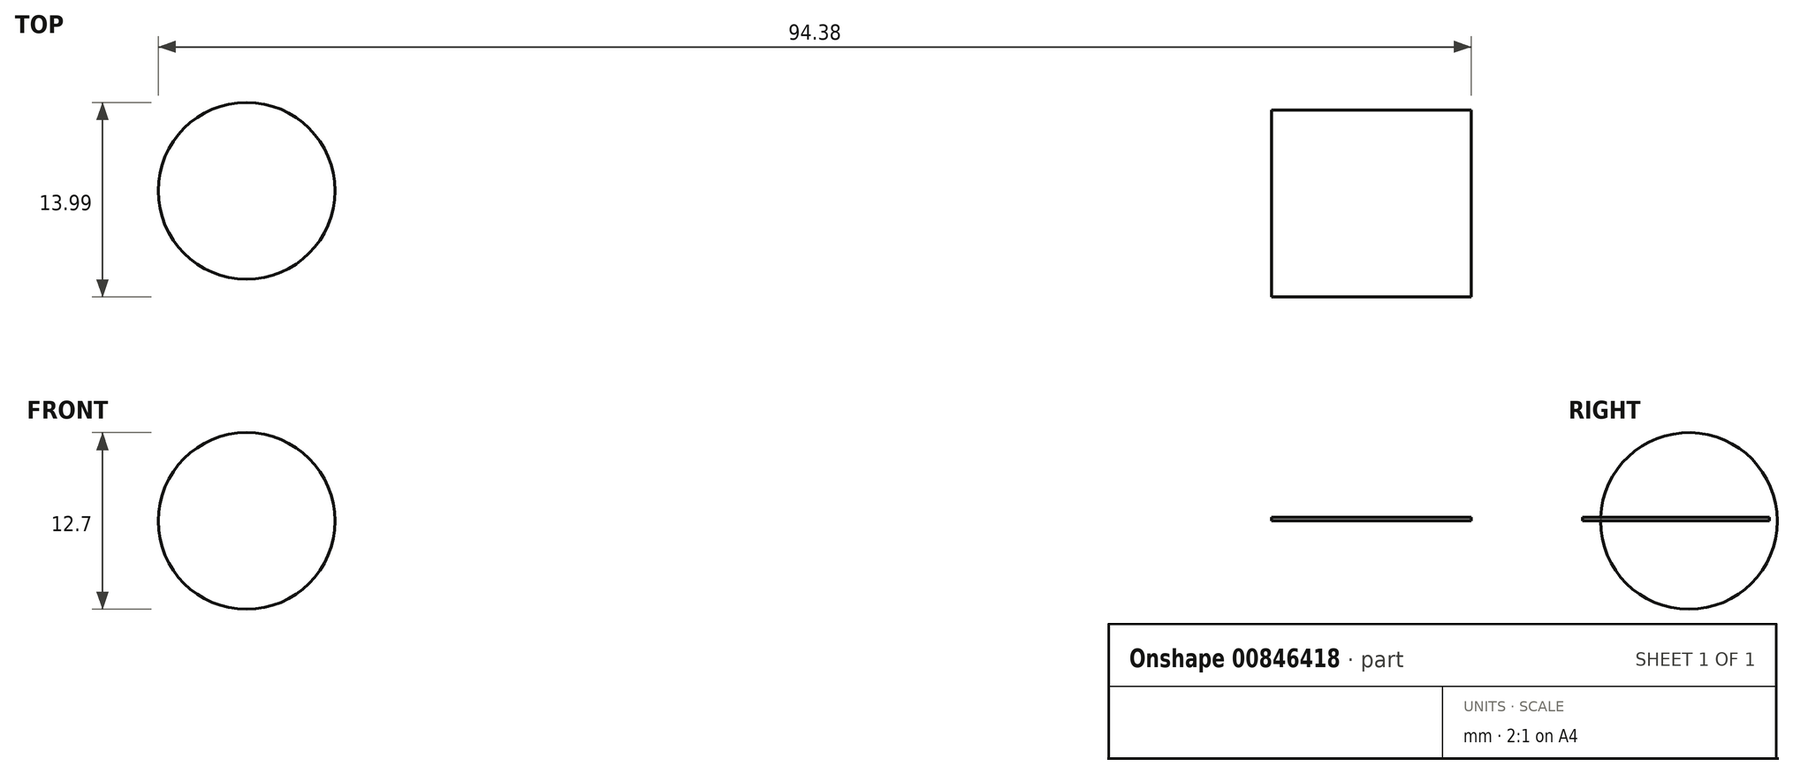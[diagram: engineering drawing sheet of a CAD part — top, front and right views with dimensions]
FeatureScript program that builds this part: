
annotation { "Feature Type Name" : "Feature", "Feature Type Description" : "" }
export const myFeature = defineFeature(function(context is Context, id is Id, definition is map)
    precondition{}
    {
        {
            var Q0;
            Q0=qCreatedBy(makeId("Top.planeOp"),FACE);
            var sketch = newSketch(context, id + "F0", { "sketchPlane" : qUnion([Q0])});
            skArc(sketch, "E0", {"start": v(-102.85, 45.29) * mm, "mid": v(-109.2, 38.94) * mm, "end": v(-102.85, 32.59) * mm});
            skLineSegment(sketch, "E1", {"start": v(-102.85, 45.29) * mm, "end": v(-102.85, 32.59) * mm});
            skSolve(sketch);
        }
        {
            var Q0;
            Q0=makeQuery(id+"F0.imprint","IMPRINT",FACE,{"disambiguationData":[TD([[makeQuery(id+"F0.imprint","IMPRINT",EDGE,{"derivedFrom":sQuery(id+"F0.wireOp",EDGE,"E0")}),1.0]])]});
            var Q1;
            Q1=sQuery(id+"F0.wireOp",EDGE,"E1");
            revolve(context, id + "F1", {"surfaceOperationType" : NewSurfaceOperationType.NEW, "entities" : qUnion([Q0]), "axis" : qUnion([Q1]), "revolveType" : RevolveType.FULL});
        }
        {
            var Q0;
            Q0=qCreatedBy(makeId("Top.planeOp"),FACE);
            var sketch = newSketch(context, id + "F2", { "sketchPlane" : qUnion([Q0])});
            skLineSegment(sketch, "E2.bottom", {"start": v(-29.17, 44.74) * mm, "end": v(-14.82, 44.74) * mm});
            skLineSegment(sketch, "E2.top", {"start": v(-29.17, 31.3) * mm, "end": v(-14.82, 31.3) * mm});
            skLineSegment(sketch, "E2.left", {"start": v(-29.17, 44.74) * mm, "end": v(-29.17, 31.3) * mm});
            skLineSegment(sketch, "E2.right", {"start": v(-14.82, 44.74) * mm, "end": v(-14.82, 31.3) * mm});
            skSolve(sketch);
        }
        {
            var Q0;
            Q0 = qSketchRegion(id + "F2", true);
            extrude(context, id + "F3", {"entities" : qUnion([Q0]), "depth" : 0.25 * mm, "offsetDistance" : 25.4 * mm});
        }
    });
